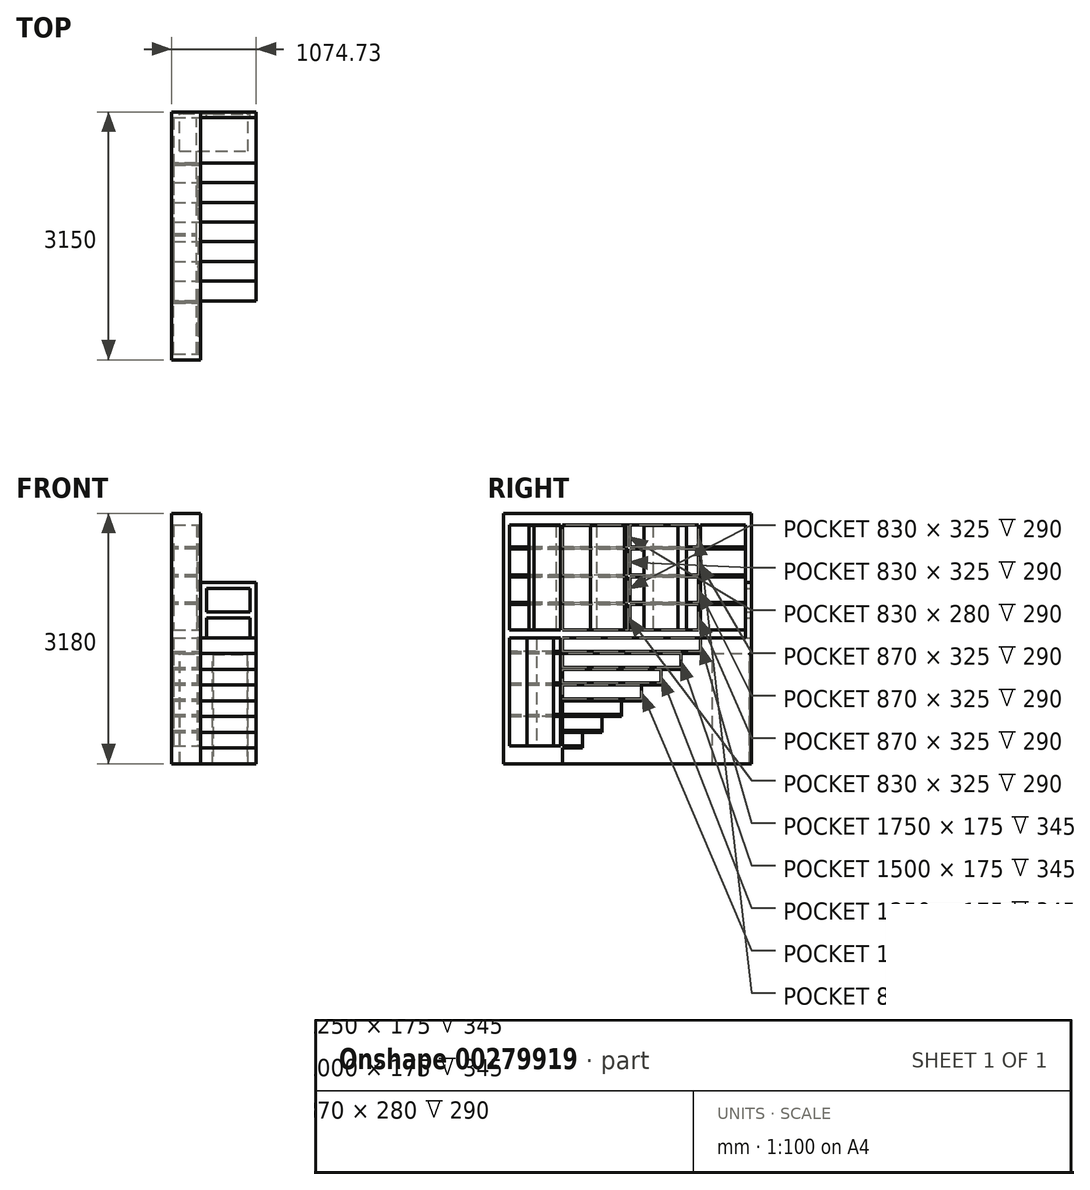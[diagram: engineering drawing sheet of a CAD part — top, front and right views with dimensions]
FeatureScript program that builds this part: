
annotation { "Feature Type Name" : "Feature", "Feature Type Description" : "" }
export const myFeature = defineFeature(function(context is Context, id is Id, definition is map)
    precondition{}
    {
        {
            var Q0;
            Q0=qCreatedBy(makeId("Top.planeOp"),FACE);
            var sketch = newSketch(context, id + "F0", { "sketchPlane" : qUnion([Q0])});
            skLineSegment(sketch, "E0.bottom", {"start": v(0, 0) * mm, "end": v(370, 0) * mm});
            skLineSegment(sketch, "E0.top", {"start": v(0, 3150) * mm, "end": v(370, 3150) * mm});
            skLineSegment(sketch, "E0.left", {"start": v(0, 0) * mm, "end": v(0, 3150) * mm});
            skLineSegment(sketch, "E0.right", {"start": v(370, 0) * mm, "end": v(370, 3150) * mm});
            skLineSegment(sketch, "E1", {"start": v(-177.4, 3270) * mm, "end": v(552.89, 3270) * mm, "construction": true});
            skSolve(sketch);
        }
        {
            var Q0;
            Q0 = qSketchRegion(id + "F0", true);
            extrude(context, id + "F1", {"entities" : qUnion([Q0]), "depth" : 3180 * mm});
        }
        {
            var Q0;
            Q0=makeQuery(id+"F1.opExtrude","SWEPT_FACE",FACE,{"disambiguationData":[OSD([sQuery(id+"F0.wireOp",EDGE,"E0.right")])]});
            var sketch = newSketch(context, id + "F2", { "sketchPlane" : qUnion([Q0])});
            skLineSegment(sketch, "E2.bottom", {"start": v(3150, 0) * mm, "end": v(750, 0) * mm});
            skLineSegment(sketch, "E2.top", {"start": v(2750, 1600) * mm, "end": v(2500, 1600) * mm});
            skLineSegment(sketch, "E2.right", {"start": v(750, 200) * mm, "end": v(750, 0) * mm});
            skLineSegment(sketch, "E3", {"start": v(750, 0) * mm, "end": v(2750, 1600) * mm, "construction": true});
            skLineSegment(sketch, "E4.0.1.0", {"start": v(1000, 200) * mm, "end": v(750, 200) * mm});
            skLineSegment(sketch, "E4.0.2.0", {"start": v(1250, 400) * mm, "end": v(1000, 400) * mm});
            skLineSegment(sketch, "E4.0.3.0", {"start": v(1500, 600) * mm, "end": v(1250, 600) * mm});
            skLineSegment(sketch, "E4.0.4.0", {"start": v(1750, 800) * mm, "end": v(1500, 800) * mm});
            skLineSegment(sketch, "E4.0.5.0", {"start": v(2000, 1000) * mm, "end": v(1750, 1000) * mm});
            skLineSegment(sketch, "E4.0.6.0", {"start": v(2250, 1200) * mm, "end": v(2000, 1200) * mm});
            skLineSegment(sketch, "E4.0.7.0", {"start": v(2500, 1400) * mm, "end": v(2250, 1400) * mm});
            skLineSegment(sketch, "E4.direction1", {"start": v(750, 0) * mm, "end": v(1805.34, 0) * mm, "construction": true});
            skLineSegment(sketch, "E4.direction2", {"start": v(750, 0) * mm, "end": v(750, 200) * mm, "construction": true});
            skLineSegment(sketch, "E5", {"start": v(1000, 200) * mm, "end": v(1000, 400) * mm});
            skLineSegment(sketch, "E6", {"start": v(1250, 400) * mm, "end": v(1250, 600) * mm});
            skLineSegment(sketch, "E7", {"start": v(1500, 600) * mm, "end": v(1500, 800) * mm});
            skLineSegment(sketch, "E8", {"start": v(2000, 1000) * mm, "end": v(2000, 1200) * mm});
            skLineSegment(sketch, "E9", {"start": v(2250, 1200) * mm, "end": v(2250, 1400) * mm});
            skLineSegment(sketch, "E10", {"start": v(2500, 1400) * mm, "end": v(2500, 1600) * mm});
            skLineSegment(sketch, "E11", {"start": v(2750, 1600) * mm, "end": v(3150, 1600) * mm});
            skLineSegment(sketch, "E12", {"start": v(3150, 1600) * mm, "end": v(3150, 0) * mm});
            skLineSegment(sketch, "E13", {"start": v(1750, 800) * mm, "end": v(1750, 1000) * mm});
            skPoint(sketch, "E14.orphan", {"position": v(750, 400) * mm});
            skPoint(sketch, "E15.orphan", {"position": v(750, 600) * mm});
            skPoint(sketch, "E16.orphan", {"position": v(750, 1000) * mm});
            skPoint(sketch, "E17.orphan", {"position": v(750, 1200) * mm});
            skPoint(sketch, "E18.orphan", {"position": v(750, 1400) * mm});
            skPoint(sketch, "E19.orphan", {"position": v(3150, 1400) * mm});
            skPoint(sketch, "E20.orphan", {"position": v(3150, 1200) * mm});
            skPoint(sketch, "E21.orphan", {"position": v(3150, 1000) * mm});
            skPoint(sketch, "E22.orphan", {"position": v(3150, 600) * mm});
            skPoint(sketch, "E23.orphan", {"position": v(3150, 400) * mm});
            skPoint(sketch, "E24.orphan", {"position": v(3150, 200) * mm});
            skPoint(sketch, "E25.orphan", {"position": v(3150, 800) * mm});
            skSolve(sketch);
        }
        {
            var Q0;
            Q0 = qSketchRegion(id + "F2", true);
            extrude(context, id + "F3", {"entities" : qUnion([Q0]), "operationType" : NewBodyOperationType.ADD, "depth" : 700 * mm});
        }
        {
            var Q0;
            Q0=qCreatedBy(makeId("Right.planeOp"),FACE);
            cPlane(context, id + "F4", {"entities" : qUnion([Q0]), "cplaneType" : CPlaneType.OFFSET, "offset" : 25 * mm, "width" : 150 * mm, "height" : 150 * mm});
        }
        {
            var Q0;
            Q0=makeQuery(id+"F1.opExtrude","SWEPT_FACE",FACE,{"disambiguationData":[OSD([sQuery(id+"F0.wireOp",EDGE,"E0.right")])]});
            var sketch = newSketch(context, id + "F5", { "sketchPlane" : qUnion([Q0])});
            skLineSegment(sketch, "E26.bottom", {"start": v(750, 400) * mm, "end": v(1000, 400) * mm});
            skLineSegment(sketch, "E26.top", {"start": v(750, 225) * mm, "end": v(1000, 225) * mm});
            skLineSegment(sketch, "E26.left", {"start": v(750, 400) * mm, "end": v(750, 225) * mm});
            skLineSegment(sketch, "E26.right", {"start": v(1000, 400) * mm, "end": v(1000, 225) * mm});
            skLineSegment(sketch, "E27.0.1.0", {"start": v(1000, 600) * mm, "end": v(1000, 425) * mm});
            skLineSegment(sketch, "E27.0.1.1", {"start": v(750, 600) * mm, "end": v(750, 425) * mm});
            skLineSegment(sketch, "E27.0.1.2", {"start": v(750, 425) * mm, "end": v(1000, 425) * mm});
            skLineSegment(sketch, "E27.0.1.3", {"start": v(750, 600) * mm, "end": v(1000, 600) * mm});
            skLineSegment(sketch, "E27.0.2.0", {"start": v(1000, 800) * mm, "end": v(1000, 625) * mm});
            skLineSegment(sketch, "E27.0.2.1", {"start": v(750, 800) * mm, "end": v(750, 625) * mm});
            skLineSegment(sketch, "E27.0.2.2", {"start": v(750, 625) * mm, "end": v(1000, 625) * mm});
            skLineSegment(sketch, "E27.0.2.3", {"start": v(750, 800) * mm, "end": v(1000, 800) * mm});
            skLineSegment(sketch, "E27.0.3.0", {"start": v(1000, 1000) * mm, "end": v(1000, 825) * mm});
            skLineSegment(sketch, "E27.0.3.1", {"start": v(750, 1000) * mm, "end": v(750, 825) * mm});
            skLineSegment(sketch, "E27.0.3.2", {"start": v(750, 825) * mm, "end": v(1000, 825) * mm});
            skLineSegment(sketch, "E27.0.3.3", {"start": v(750, 1000) * mm, "end": v(1000, 1000) * mm});
            skLineSegment(sketch, "E27.0.4.0", {"start": v(1000, 1200) * mm, "end": v(1000, 1025) * mm});
            skLineSegment(sketch, "E27.0.4.1", {"start": v(750, 1200) * mm, "end": v(750, 1025) * mm});
            skLineSegment(sketch, "E27.0.4.2", {"start": v(750, 1025) * mm, "end": v(1000, 1025) * mm});
            skLineSegment(sketch, "E27.0.4.3", {"start": v(750, 1200) * mm, "end": v(1000, 1200) * mm});
            skLineSegment(sketch, "E27.0.5.0", {"start": v(1000, 1400) * mm, "end": v(1000, 1225) * mm});
            skLineSegment(sketch, "E27.0.5.1", {"start": v(750, 1400) * mm, "end": v(750, 1225) * mm});
            skLineSegment(sketch, "E27.0.5.2", {"start": v(750, 1225) * mm, "end": v(1000, 1225) * mm});
            skLineSegment(sketch, "E27.0.5.3", {"start": v(750, 1400) * mm, "end": v(1000, 1400) * mm});
            skLineSegment(sketch, "E27.0.6.0", {"start": v(1000, 1600) * mm, "end": v(1000, 1425) * mm});
            skLineSegment(sketch, "E27.0.6.1", {"start": v(750, 1600) * mm, "end": v(750, 1425) * mm});
            skLineSegment(sketch, "E27.0.6.2", {"start": v(750, 1425) * mm, "end": v(1000, 1425) * mm});
            skLineSegment(sketch, "E27.0.6.3", {"start": v(750, 1600) * mm, "end": v(1000, 1600) * mm});
            skLineSegment(sketch, "E27.1.1.0", {"start": v(1250, 600) * mm, "end": v(1250, 425) * mm});
            skLineSegment(sketch, "E27.1.1.1", {"start": v(1000, 600) * mm, "end": v(1000, 425) * mm});
            skLineSegment(sketch, "E27.1.1.2", {"start": v(1000, 425) * mm, "end": v(1250, 425) * mm});
            skLineSegment(sketch, "E27.1.1.3", {"start": v(1000, 600) * mm, "end": v(1250, 600) * mm});
            skLineSegment(sketch, "E27.1.2.0", {"start": v(1250, 800) * mm, "end": v(1250, 625) * mm});
            skLineSegment(sketch, "E27.1.2.1", {"start": v(1000, 800) * mm, "end": v(1000, 625) * mm});
            skLineSegment(sketch, "E27.1.2.2", {"start": v(1000, 625) * mm, "end": v(1250, 625) * mm});
            skLineSegment(sketch, "E27.1.2.3", {"start": v(1000, 800) * mm, "end": v(1250, 800) * mm});
            skLineSegment(sketch, "E27.1.3.0", {"start": v(1250, 1000) * mm, "end": v(1250, 825) * mm});
            skLineSegment(sketch, "E27.1.3.1", {"start": v(1000, 1000) * mm, "end": v(1000, 825) * mm});
            skLineSegment(sketch, "E27.1.3.2", {"start": v(1000, 825) * mm, "end": v(1250, 825) * mm});
            skLineSegment(sketch, "E27.1.3.3", {"start": v(1000, 1000) * mm, "end": v(1250, 1000) * mm});
            skLineSegment(sketch, "E27.1.4.0", {"start": v(1250, 1200) * mm, "end": v(1250, 1025) * mm});
            skLineSegment(sketch, "E27.1.4.1", {"start": v(1000, 1200) * mm, "end": v(1000, 1025) * mm});
            skLineSegment(sketch, "E27.1.4.2", {"start": v(1000, 1025) * mm, "end": v(1250, 1025) * mm});
            skLineSegment(sketch, "E27.1.4.3", {"start": v(1000, 1200) * mm, "end": v(1250, 1200) * mm});
            skLineSegment(sketch, "E27.1.5.0", {"start": v(1250, 1400) * mm, "end": v(1250, 1225) * mm});
            skLineSegment(sketch, "E27.1.5.1", {"start": v(1000, 1400) * mm, "end": v(1000, 1225) * mm});
            skLineSegment(sketch, "E27.1.5.2", {"start": v(1000, 1225) * mm, "end": v(1250, 1225) * mm});
            skLineSegment(sketch, "E27.1.5.3", {"start": v(1000, 1400) * mm, "end": v(1250, 1400) * mm});
            skLineSegment(sketch, "E27.1.6.0", {"start": v(1250, 1600) * mm, "end": v(1250, 1425) * mm});
            skLineSegment(sketch, "E27.1.6.1", {"start": v(1000, 1600) * mm, "end": v(1000, 1425) * mm});
            skLineSegment(sketch, "E27.1.6.2", {"start": v(1000, 1425) * mm, "end": v(1250, 1425) * mm});
            skLineSegment(sketch, "E27.1.6.3", {"start": v(1000, 1600) * mm, "end": v(1250, 1600) * mm});
            skLineSegment(sketch, "E27.2.1.1", {"start": v(1250, 600) * mm, "end": v(1250, 425) * mm});
            skLineSegment(sketch, "E27.2.1.3", {"start": v(1250, 600) * mm, "end": v(1500, 600) * mm});
            skLineSegment(sketch, "E27.2.2.0", {"start": v(1500, 800) * mm, "end": v(1500, 625) * mm});
            skLineSegment(sketch, "E27.2.2.1", {"start": v(1250, 800) * mm, "end": v(1250, 625) * mm});
            skLineSegment(sketch, "E27.2.2.2", {"start": v(1250, 625) * mm, "end": v(1500, 625) * mm});
            skLineSegment(sketch, "E27.2.2.3", {"start": v(1250, 800) * mm, "end": v(1500, 800) * mm});
            skLineSegment(sketch, "E27.2.3.0", {"start": v(1500, 1000) * mm, "end": v(1500, 825) * mm});
            skLineSegment(sketch, "E27.2.3.1", {"start": v(1250, 1000) * mm, "end": v(1250, 825) * mm});
            skLineSegment(sketch, "E27.2.3.2", {"start": v(1250, 825) * mm, "end": v(1500, 825) * mm});
            skLineSegment(sketch, "E27.2.3.3", {"start": v(1250, 1000) * mm, "end": v(1500, 1000) * mm});
            skLineSegment(sketch, "E27.2.4.0", {"start": v(1500, 1200) * mm, "end": v(1500, 1025) * mm});
            skLineSegment(sketch, "E27.2.4.1", {"start": v(1250, 1200) * mm, "end": v(1250, 1025) * mm});
            skLineSegment(sketch, "E27.2.4.2", {"start": v(1250, 1025) * mm, "end": v(1500, 1025) * mm});
            skLineSegment(sketch, "E27.2.4.3", {"start": v(1250, 1200) * mm, "end": v(1500, 1200) * mm});
            skLineSegment(sketch, "E27.2.5.0", {"start": v(1500, 1400) * mm, "end": v(1500, 1225) * mm});
            skLineSegment(sketch, "E27.2.5.1", {"start": v(1250, 1400) * mm, "end": v(1250, 1225) * mm});
            skLineSegment(sketch, "E27.2.5.2", {"start": v(1250, 1225) * mm, "end": v(1500, 1225) * mm});
            skLineSegment(sketch, "E27.2.5.3", {"start": v(1250, 1400) * mm, "end": v(1500, 1400) * mm});
            skLineSegment(sketch, "E27.2.6.0", {"start": v(1500, 1600) * mm, "end": v(1500, 1425) * mm});
            skLineSegment(sketch, "E27.2.6.1", {"start": v(1250, 1600) * mm, "end": v(1250, 1425) * mm});
            skLineSegment(sketch, "E27.2.6.2", {"start": v(1250, 1425) * mm, "end": v(1500, 1425) * mm});
            skLineSegment(sketch, "E27.2.6.3", {"start": v(1250, 1600) * mm, "end": v(1500, 1600) * mm});
            skLineSegment(sketch, "E27.3.2.1", {"start": v(1500, 800) * mm, "end": v(1500, 625) * mm});
            skLineSegment(sketch, "E27.3.2.3", {"start": v(1500, 800) * mm, "end": v(1750, 800) * mm});
            skLineSegment(sketch, "E27.3.3.0", {"start": v(1750, 1000) * mm, "end": v(1750, 825) * mm});
            skLineSegment(sketch, "E27.3.3.1", {"start": v(1500, 1000) * mm, "end": v(1500, 825) * mm});
            skLineSegment(sketch, "E27.3.3.2", {"start": v(1500, 825) * mm, "end": v(1750, 825) * mm});
            skLineSegment(sketch, "E27.3.3.3", {"start": v(1500, 1000) * mm, "end": v(1750, 1000) * mm});
            skLineSegment(sketch, "E27.3.4.0", {"start": v(1750, 1200) * mm, "end": v(1750, 1025) * mm});
            skLineSegment(sketch, "E27.3.4.1", {"start": v(1500, 1200) * mm, "end": v(1500, 1025) * mm});
            skLineSegment(sketch, "E27.3.4.2", {"start": v(1500, 1025) * mm, "end": v(1750, 1025) * mm});
            skLineSegment(sketch, "E27.3.4.3", {"start": v(1500, 1200) * mm, "end": v(1750, 1200) * mm});
            skLineSegment(sketch, "E27.3.5.0", {"start": v(1750, 1400) * mm, "end": v(1750, 1225) * mm});
            skLineSegment(sketch, "E27.3.5.1", {"start": v(1500, 1400) * mm, "end": v(1500, 1225) * mm});
            skLineSegment(sketch, "E27.3.5.2", {"start": v(1500, 1225) * mm, "end": v(1750, 1225) * mm});
            skLineSegment(sketch, "E27.3.5.3", {"start": v(1500, 1400) * mm, "end": v(1750, 1400) * mm});
            skLineSegment(sketch, "E27.3.6.0", {"start": v(1750, 1600) * mm, "end": v(1750, 1425) * mm});
            skLineSegment(sketch, "E27.3.6.1", {"start": v(1500, 1600) * mm, "end": v(1500, 1425) * mm});
            skLineSegment(sketch, "E27.3.6.2", {"start": v(1500, 1425) * mm, "end": v(1750, 1425) * mm});
            skLineSegment(sketch, "E27.3.6.3", {"start": v(1500, 1600) * mm, "end": v(1750, 1600) * mm});
            skLineSegment(sketch, "E27.4.3.1", {"start": v(1750, 1000) * mm, "end": v(1750, 825) * mm});
            skLineSegment(sketch, "E27.4.3.3", {"start": v(1750, 1000) * mm, "end": v(2000, 1000) * mm});
            skLineSegment(sketch, "E27.4.4.0", {"start": v(2000, 1200) * mm, "end": v(2000, 1025) * mm});
            skLineSegment(sketch, "E27.4.4.1", {"start": v(1750, 1200) * mm, "end": v(1750, 1025) * mm});
            skLineSegment(sketch, "E27.4.4.2", {"start": v(1750, 1025) * mm, "end": v(2000, 1025) * mm});
            skLineSegment(sketch, "E27.4.4.3", {"start": v(1750, 1200) * mm, "end": v(2000, 1200) * mm});
            skLineSegment(sketch, "E27.4.5.0", {"start": v(2000, 1400) * mm, "end": v(2000, 1225) * mm});
            skLineSegment(sketch, "E27.4.5.1", {"start": v(1750, 1400) * mm, "end": v(1750, 1225) * mm});
            skLineSegment(sketch, "E27.4.5.2", {"start": v(1750, 1225) * mm, "end": v(2000, 1225) * mm});
            skLineSegment(sketch, "E27.4.5.3", {"start": v(1750, 1400) * mm, "end": v(2000, 1400) * mm});
            skLineSegment(sketch, "E27.4.6.0", {"start": v(2000, 1600) * mm, "end": v(2000, 1425) * mm});
            skLineSegment(sketch, "E27.4.6.1", {"start": v(1750, 1600) * mm, "end": v(1750, 1425) * mm});
            skLineSegment(sketch, "E27.4.6.2", {"start": v(1750, 1425) * mm, "end": v(2000, 1425) * mm});
            skLineSegment(sketch, "E27.4.6.3", {"start": v(1750, 1600) * mm, "end": v(2000, 1600) * mm});
            skLineSegment(sketch, "E27.5.4.1", {"start": v(2000, 1200) * mm, "end": v(2000, 1025) * mm});
            skLineSegment(sketch, "E27.5.4.3", {"start": v(2000, 1200) * mm, "end": v(2250, 1200) * mm});
            skLineSegment(sketch, "E27.5.5.0", {"start": v(2250, 1400) * mm, "end": v(2250, 1225) * mm});
            skLineSegment(sketch, "E27.5.5.1", {"start": v(2000, 1400) * mm, "end": v(2000, 1225) * mm});
            skLineSegment(sketch, "E27.5.5.2", {"start": v(2000, 1225) * mm, "end": v(2250, 1225) * mm});
            skLineSegment(sketch, "E27.5.5.3", {"start": v(2000, 1400) * mm, "end": v(2250, 1400) * mm});
            skLineSegment(sketch, "E27.5.6.0", {"start": v(2250, 1600) * mm, "end": v(2250, 1425) * mm});
            skLineSegment(sketch, "E27.5.6.1", {"start": v(2000, 1600) * mm, "end": v(2000, 1425) * mm});
            skLineSegment(sketch, "E27.5.6.2", {"start": v(2000, 1425) * mm, "end": v(2250, 1425) * mm});
            skLineSegment(sketch, "E27.5.6.3", {"start": v(2000, 1600) * mm, "end": v(2250, 1600) * mm});
            skLineSegment(sketch, "E27.6.5.1", {"start": v(2250, 1400) * mm, "end": v(2250, 1225) * mm});
            skLineSegment(sketch, "E27.6.5.3", {"start": v(2250, 1400) * mm, "end": v(2500, 1400) * mm});
            skLineSegment(sketch, "E27.6.6.0", {"start": v(2500, 1600) * mm, "end": v(2500, 1425) * mm});
            skLineSegment(sketch, "E27.6.6.1", {"start": v(2250, 1600) * mm, "end": v(2250, 1425) * mm});
            skLineSegment(sketch, "E27.6.6.2", {"start": v(2250, 1425) * mm, "end": v(2500, 1425) * mm});
            skLineSegment(sketch, "E27.6.6.3", {"start": v(2250, 1600) * mm, "end": v(2500, 1600) * mm});
            skLineSegment(sketch, "E27.direction1", {"start": v(750, 225) * mm, "end": v(1000, 225) * mm, "construction": true});
            skLineSegment(sketch, "E27.direction2", {"start": v(750, 225) * mm, "end": v(750, 425) * mm, "construction": true});
            skSolve(sketch);
        }
        {
            var Q0;
            Q0 = qSketchRegion(id + "F5", true);
            var Q1;
            Q1=qCreatedBy(id+"F4.planeOp",FACE);
            extrude(context, id + "F6", {"entities" : qUnion([Q0]), "operationType" : NewBodyOperationType.REMOVE, "endBound" : BoundingType.UP_TO_SURFACE, "oppositeDirection" : true, "endBoundEntityFace" : qUnion([Q1]), "depth" : 25 * mm});
        }
        {
            var Q0;
            Q0=makeQuery(id+"F1.opExtrude","SWEPT_FACE",FACE,{"disambiguationData":[OSD([sQuery(id+"F0.wireOp",EDGE,"E0.right")])]});
            var sketch = newSketch(context, id + "F7", { "sketchPlane" : qUnion([Q0])});
            skLineSegment(sketch, "E28.bottom", {"start": v(725, 225) * mm, "end": v(75, 225) * mm});
            skLineSegment(sketch, "E28.top", {"start": v(725, 600) * mm, "end": v(75, 600) * mm});
            skLineSegment(sketch, "E28.left", {"start": v(725, 225) * mm, "end": v(725, 600) * mm});
            skLineSegment(sketch, "E28.right", {"start": v(75, 225) * mm, "end": v(75, 600) * mm});
            skLineSegment(sketch, "E29.0.1.0", {"start": v(725, 625) * mm, "end": v(75, 625) * mm});
            skLineSegment(sketch, "E29.0.1.1", {"start": v(725, 1000) * mm, "end": v(75, 1000) * mm});
            skLineSegment(sketch, "E29.0.1.2", {"start": v(725, 625) * mm, "end": v(725, 1000) * mm});
            skLineSegment(sketch, "E29.0.1.3", {"start": v(75, 625) * mm, "end": v(75, 1000) * mm});
            skLineSegment(sketch, "E29.0.2.0", {"start": v(725, 1025) * mm, "end": v(75, 1025) * mm});
            skLineSegment(sketch, "E29.0.2.1", {"start": v(725, 1400) * mm, "end": v(75, 1400) * mm});
            skLineSegment(sketch, "E29.0.2.2", {"start": v(725, 1025) * mm, "end": v(725, 1400) * mm});
            skLineSegment(sketch, "E29.0.2.3", {"start": v(75, 1025) * mm, "end": v(75, 1400) * mm});
            skLineSegment(sketch, "E29.direction1", {"start": v(50, 225) * mm, "end": v(75, 225) * mm, "construction": true});
            skLineSegment(sketch, "E29.direction2", {"start": v(75, 225) * mm, "end": v(75, 625) * mm, "construction": true});
            skLineSegment(sketch, "E30.bottom", {"start": v(725, 1425) * mm, "end": v(75, 1425) * mm});
            skLineSegment(sketch, "E30.top", {"start": v(725, 1600) * mm, "end": v(75, 1600) * mm});
            skLineSegment(sketch, "E30.left", {"start": v(725, 1425) * mm, "end": v(725, 1600) * mm});
            skLineSegment(sketch, "E30.right", {"start": v(75, 1425) * mm, "end": v(75, 1600) * mm});
            skSolve(sketch);
        }
        {
            var Q0;
            Q0 = qSketchRegion(id + "F7", true);
            var Q1;
            Q1=qCreatedBy(id+"F4.planeOp",FACE);
            extrude(context, id + "F8", {"entities" : qUnion([Q0]), "operationType" : NewBodyOperationType.REMOVE, "endBound" : BoundingType.UP_TO_SURFACE, "oppositeDirection" : true, "endBoundEntityFace" : qUnion([Q1]), "depth" : 25 * mm});
        }
        {
            var Q0;
            Q0=makeQuery(id+"F1.opExtrude","SWEPT_FACE",FACE,{"disambiguationData":[OSD([sQuery(id+"F0.wireOp",EDGE,"E0.right")])]});
            var sketch = newSketch(context, id + "F9", { "sketchPlane" : qUnion([Q0])});
            skLineSegment(sketch, "E31.bottom", {"start": v(2500, 1700) * mm, "end": v(3075, 1700) * mm});
            skLineSegment(sketch, "E31.top", {"start": v(2500, 3030) * mm, "end": v(3075, 3030) * mm});
            skLineSegment(sketch, "E31.left", {"start": v(2500, 1700) * mm, "end": v(2500, 3030) * mm});
            skLineSegment(sketch, "E31.right", {"start": v(3075, 1700) * mm, "end": v(3075, 3030) * mm});
            skLineSegment(sketch, "E32.bottom", {"start": v(725, 1700) * mm, "end": v(75, 1700) * mm});
            skLineSegment(sketch, "E32.top", {"start": v(725, 3030) * mm, "end": v(75, 3030) * mm});
            skLineSegment(sketch, "E32.left", {"start": v(725, 1700) * mm, "end": v(725, 3030) * mm});
            skLineSegment(sketch, "E32.right", {"start": v(75, 1700) * mm, "end": v(75, 3030) * mm});
            skLineSegment(sketch, "E33.bottom", {"start": v(750, 1700) * mm, "end": v(2475, 1700) * mm});
            skLineSegment(sketch, "E33.top", {"start": v(750, 3030) * mm, "end": v(2475, 3030) * mm});
            skLineSegment(sketch, "E33.left", {"start": v(750, 1700) * mm, "end": v(750, 3030) * mm});
            skLineSegment(sketch, "E33.right", {"start": v(2475, 1700) * mm, "end": v(2475, 3030) * mm});
            skSolve(sketch);
        }
        {
            var Q0;
            Q0=makeQuery(id+"F9.imprint","IMPRINT",FACE,{"disambiguationData":[TD([[makeQuery(id+"F9.imprint","IMPRINT",EDGE,{"derivedFrom":sQuery(id+"F9.wireOp",EDGE,"E31.bottom")}),-1.0]])]});
            var sketch = newSketch(context, id + "F10", { "sketchPlane" : qUnion([Q0])});
            skLineSegment(sketch, "E34.bottom", {"start": v(75, 1425) * mm, "end": v(725, 1425) * mm});
            skLineSegment(sketch, "E34.top", {"start": v(75, 600) * mm, "end": v(725, 600) * mm});
            skLineSegment(sketch, "E34.left", {"start": v(75, 1425) * mm, "end": v(75, 600) * mm});
            skLineSegment(sketch, "E34.right", {"start": v(725, 1425) * mm, "end": v(725, 600) * mm});
            skSolve(sketch);
        }
        {
            var Q0;
            Q0 = qSketchRegion(id + "F10", true);
            extrude(context, id + "F11", {"entities" : qUnion([Q0]), "operationType" : NewBodyOperationType.REMOVE, "oppositeDirection" : true, "depth" : 55 * mm});
        }
        {
            var Q0;
            Q0 = qSketchRegion(id + "F9", true);
            var Q1;
            Q1=qCreatedBy(id+"F4.planeOp",FACE);
            extrude(context, id + "F12", {"entities" : qUnion([Q0]), "operationType" : NewBodyOperationType.REMOVE, "endBound" : BoundingType.UP_TO_SURFACE, "oppositeDirection" : true, "endBoundEntityFace" : qUnion([Q1]), "depth" : 25 * mm});
        }
        {
            var Q0;
            {var subQ0=sQuery(id+"F10.wireOp",EDGE,"E34.left");var subQ1=sQuery(id+"F10.wireOp",EDGE,"E34.right");Q0=makeQuery(id+"F11.boolean.opBoolean","COPY",FACE,{"disambiguationData":[TD([makeQuery(id+"F8.boolean.opBoolean","COPY",FACE,{"derivedFrom":makeQuery(id+"F8.opExtrude","SWEPT_FACE",FACE,{"disambiguationData":[OSD([sQuery(id+"F7.wireOp",EDGE,"E29.0.2.1")])]})})])],"derivedFrom":makeQuery(id+"F11.opExtrude","CAP_FACE",FACE,{"disambiguationData":[OSD([sQuery(id+"F10.wireOp",EDGE,"E34.bottom"),sQuery(id+"F10.wireOp",EDGE,"E34.top"),subQ0,subQ1])],"isStart":false})});}
            var sketch = newSketch(context, id + "F13", { "sketchPlane" : qUnion([Q0])});
            skLineSegment(sketch, "E35.bottom", {"start": v(75, 2025) * mm, "end": v(1580, 2025) * mm});
            skLineSegment(sketch, "E35.top", {"start": v(75, 2050) * mm, "end": v(1580, 2050) * mm});
            skLineSegment(sketch, "E35.left", {"start": v(75, 2025) * mm, "end": v(75, 2050) * mm});
            skLineSegment(sketch, "E35.right", {"start": v(3075, 2025) * mm, "end": v(3075, 2050) * mm});
            skLineSegment(sketch, "E36.0.1.0", {"start": v(75, 2400) * mm, "end": v(1580, 2400) * mm});
            skLineSegment(sketch, "E36.0.1.1", {"start": v(75, 2375) * mm, "end": v(1580, 2375) * mm});
            skLineSegment(sketch, "E36.0.1.2", {"start": v(3075, 2375) * mm, "end": v(3075, 2400) * mm});
            skLineSegment(sketch, "E36.0.1.3", {"start": v(75, 2375) * mm, "end": v(75, 2400) * mm});
            skLineSegment(sketch, "E36.0.2.0", {"start": v(75, 2750) * mm, "end": v(1580, 2750) * mm});
            skLineSegment(sketch, "E36.0.2.1", {"start": v(75, 2725) * mm, "end": v(1580, 2725) * mm});
            skLineSegment(sketch, "E36.0.2.2", {"start": v(3075, 2725) * mm, "end": v(3075, 2750) * mm});
            skLineSegment(sketch, "E36.0.2.3", {"start": v(75, 2725) * mm, "end": v(75, 2750) * mm});
            skLineSegment(sketch, "E36.direction1", {"start": v(75, 2020) * mm, "end": v(100, 2020) * mm, "construction": true});
            skLineSegment(sketch, "E36.direction2", {"start": v(75, 2020) * mm, "end": v(75, 2370) * mm, "construction": true});
            skLineSegment(sketch, "E37.bottom", {"start": v(1580, 3030) * mm, "end": v(1605, 3030) * mm});
            skLineSegment(sketch, "E37.top", {"start": v(1580, 1700) * mm, "end": v(1605, 1700) * mm});
            skLineSegment(sketch, "E37.left", {"start": v(1580, 3030) * mm, "end": v(1580, 1700) * mm});
            skLineSegment(sketch, "E37.right", {"start": v(1605, 3030) * mm, "end": v(1605, 1700) * mm});
            skLineSegment(sketch, "E38.trimOffspring", {"start": v(1605, 2050) * mm, "end": v(3075, 2050) * mm});
            skLineSegment(sketch, "E39.trimOffspring", {"start": v(1605, 2025) * mm, "end": v(3075, 2025) * mm});
            skLineSegment(sketch, "E40.trimOffspring", {"start": v(1605, 2400) * mm, "end": v(3075, 2400) * mm});
            skLineSegment(sketch, "E41.trimOffspring", {"start": v(1605, 2375) * mm, "end": v(3075, 2375) * mm});
            skLineSegment(sketch, "E42.trimOffspring", {"start": v(1605, 2750) * mm, "end": v(3075, 2750) * mm});
            skLineSegment(sketch, "E43.trimOffspring", {"start": v(1605, 2725) * mm, "end": v(3075, 2725) * mm});
            skSolve(sketch);
        }
        {
            var Q0;
            Q0 = qSketchRegion(id + "F13", true);
            var Q1;
            Q1=qCreatedBy(id+"F4.planeOp",FACE);
            extrude(context, id + "F14", {"entities" : qUnion([Q0]), "operationType" : NewBodyOperationType.ADD, "endBound" : BoundingType.UP_TO_SURFACE, "oppositeDirection" : true, "endBoundEntityFace" : qUnion([Q1]), "depth" : 25 * mm});
        }
        {
            var Q0;
            Q0=makeQuery(id+"F1.opExtrude","SWEPT_FACE",FACE,{"disambiguationData":[OSD([sQuery(id+"F0.wireOp",EDGE,"E0.right")])]});
            cPlane(context, id + "F15", {"entities" : qUnion([Q0]), "cplaneType" : CPlaneType.OFFSET, "offset" : 25 * mm, "oppositeDirection" : true, "width" : 150 * mm, "height" : 150 * mm});
        }
        {
            var Q0;
            Q0=qCreatedBy(id+"F15.planeOp",FACE);
            cPlane(context, id + "F16", {"entities" : qUnion([Q0]), "cplaneType" : CPlaneType.OFFSET, "offset" : 25 * mm, "oppositeDirection" : true, "width" : 150 * mm, "height" : 150 * mm});
        }
        {
            var Q0;
            Q0=qCreatedBy(id+"F16.planeOp",FACE);
            var sketch = newSketch(context, id + "F17", { "sketchPlane" : qUnion([Q0])});
            skLineSegment(sketch, "E44.bottom", {"start": v(75, 1595) * mm, "end": v(415, 1595) * mm});
            skLineSegment(sketch, "E44.top", {"start": v(75, 225) * mm, "end": v(415, 225) * mm});
            skLineSegment(sketch, "E44.left", {"start": v(75, 1595) * mm, "end": v(75, 225) * mm});
            skLineSegment(sketch, "E44.right", {"start": v(415, 1595) * mm, "end": v(415, 225) * mm});
            skLineSegment(sketch, "E45.bottom", {"start": v(325, 3025) * mm, "end": v(665, 3025) * mm});
            skLineSegment(sketch, "E45.top", {"start": v(325, 1700) * mm, "end": v(665, 1700) * mm});
            skLineSegment(sketch, "E45.left", {"start": v(325, 3025) * mm, "end": v(325, 1700) * mm});
            skLineSegment(sketch, "E45.right", {"start": v(665, 3025) * mm, "end": v(665, 1700) * mm});
            skLineSegment(sketch, "E46.bottom", {"start": v(750, 3025) * mm, "end": v(1180, 3025) * mm});
            skLineSegment(sketch, "E46.top", {"start": v(750, 1700) * mm, "end": v(1180, 1700) * mm});
            skLineSegment(sketch, "E46.left", {"start": v(750, 3025) * mm, "end": v(750, 1700) * mm});
            skLineSegment(sketch, "E46.right", {"start": v(1180, 3025) * mm, "end": v(1180, 1700) * mm});
            skLineSegment(sketch, "E47.bottom", {"start": v(2325, 3025) * mm, "end": v(1895, 3025) * mm});
            skLineSegment(sketch, "E47.top", {"start": v(2325, 1700) * mm, "end": v(1895, 1700) * mm});
            skLineSegment(sketch, "E47.left", {"start": v(2325, 3025) * mm, "end": v(2325, 1700) * mm});
            skLineSegment(sketch, "E47.right", {"start": v(1895, 3025) * mm, "end": v(1895, 1700) * mm});
            skSolve(sketch);
        }
        {
            var Q0;
            Q0 = qSketchRegion(id + "F17", true);
            extrude(context, id + "F18", {"entities" : qUnion([Q0]), "operationType" : NewBodyOperationType.ADD, "depth" : 20 * mm});
        }
        {
            var Q0;
            Q0=qCreatedBy(id+"F15.planeOp",FACE);
            var sketch = newSketch(context, id + "F19", { "sketchPlane" : qUnion([Q0])});
            skLineSegment(sketch, "E48.bottom", {"start": v(295, 1595) * mm, "end": v(635, 1595) * mm});
            skLineSegment(sketch, "E48.top", {"start": v(295, 225) * mm, "end": v(635, 225) * mm});
            skLineSegment(sketch, "E48.left", {"start": v(295, 1595) * mm, "end": v(295, 225) * mm});
            skLineSegment(sketch, "E48.right", {"start": v(635, 1595) * mm, "end": v(635, 225) * mm});
            skLineSegment(sketch, "E49.bottom", {"start": v(385, 3025) * mm, "end": v(725, 3025) * mm});
            skLineSegment(sketch, "E49.top", {"start": v(385, 1700) * mm, "end": v(725, 1700) * mm});
            skLineSegment(sketch, "E49.left", {"start": v(385, 3025) * mm, "end": v(385, 1700) * mm});
            skLineSegment(sketch, "E49.right", {"start": v(725, 3025) * mm, "end": v(725, 1700) * mm});
            skLineSegment(sketch, "E50.bottom", {"start": v(1105, 3025) * mm, "end": v(1535, 3025) * mm});
            skLineSegment(sketch, "E50.top", {"start": v(1105, 1700) * mm, "end": v(1535, 1700) * mm});
            skLineSegment(sketch, "E50.left", {"start": v(1105, 3025) * mm, "end": v(1105, 1700) * mm});
            skLineSegment(sketch, "E50.right", {"start": v(1535, 3025) * mm, "end": v(1535, 1700) * mm});
            skLineSegment(sketch, "E51.bottom", {"start": v(1785, 3025) * mm, "end": v(2215, 3025) * mm});
            skLineSegment(sketch, "E51.top", {"start": v(1785, 1700) * mm, "end": v(2215, 1700) * mm});
            skLineSegment(sketch, "E51.left", {"start": v(1785, 3025) * mm, "end": v(1785, 1700) * mm});
            skLineSegment(sketch, "E51.right", {"start": v(2215, 3025) * mm, "end": v(2215, 1700) * mm});
            skSolve(sketch);
        }
        {
            var Q0;
            Q0 = qSketchRegion(id + "F19", true);
            extrude(context, id + "F20", {"entities" : qUnion([Q0]), "operationType" : NewBodyOperationType.ADD, "depth" : 20 * mm});
        }
        {
            var Q0;
            Q0=makeQuery(id+"F3.boolean.opBoolean","MERGE",FACE,{"derivedFrom":[makeQuery(id+"F1.opExtrude","SWEPT_FACE",FACE,{"disambiguationData":[OSD([sQuery(id+"F0.wireOp",EDGE,"E0.top")])]}),makeQuery(id+"F3.opExtrude","SWEPT_FACE",FACE,{"disambiguationData":[OSD([sQuery(id+"F2.wireOp",EDGE,"E12")])]})]});
            var sketch = newSketch(context, id + "F21", { "sketchPlane" : qUnion([Q0])});
            skLineSegment(sketch, "E52.bottom", {"start": v(-1070, 1600) * mm, "end": v(-995, 1600) * mm});
            skLineSegment(sketch, "E52.top", {"start": v(-1070, 2300) * mm, "end": v(-370, 2300) * mm});
            skLineSegment(sketch, "E52.left", {"start": v(-1070, 1600) * mm, "end": v(-1070, 2300) * mm});
            skLineSegment(sketch, "E52.right", {"start": v(-370, 1600) * mm, "end": v(-370, 2300) * mm});
            skLineSegment(sketch, "E53.top", {"start": v(-995, 2225) * mm, "end": v(-445, 2225) * mm});
            skLineSegment(sketch, "E53.left", {"start": v(-995, 1600) * mm, "end": v(-995, 1850) * mm});
            skLineSegment(sketch, "E53.right", {"start": v(-445, 1600) * mm, "end": v(-445, 1850) * mm});
            skLineSegment(sketch, "E54.bottom", {"start": v(-995, 1925) * mm, "end": v(-445, 1925) * mm});
            skLineSegment(sketch, "E54.top", {"start": v(-995, 1850) * mm, "end": v(-445, 1850) * mm});
            skLineSegment(sketch, "E55.trimOffspring", {"start": v(-995, 1925) * mm, "end": v(-995, 2225) * mm});
            skLineSegment(sketch, "E56.trimOffspring", {"start": v(-445, 1925) * mm, "end": v(-445, 2225) * mm});
            skLineSegment(sketch, "E57.trimOffspring", {"start": v(-445, 1600) * mm, "end": v(-370, 1600) * mm});
            skSolve(sketch);
        }
        {
            var Q0;
            Q0 = qSketchRegion(id + "F21", true);
            var Q1;
            Q1=makeQuery(id+"F12.boolean.opBoolean","COPY",FACE,{"derivedFrom":makeQuery(id+"F12.opExtrude","SWEPT_FACE",FACE,{"disambiguationData":[OSD([sQuery(id+"F9.wireOp",EDGE,"E31.right")])]})});
            extrude(context, id + "F22", {"entities" : qUnion([Q0]), "operationType" : NewBodyOperationType.ADD, "endBound" : BoundingType.UP_TO_SURFACE, "oppositeDirection" : true, "endBoundEntityFace" : qUnion([Q1]), "depth" : 25 * mm});
        }
        {
            var Q0;
            Q0=makeQuery(id+"F22.boolean.opBoolean","MERGE",FACE,{"derivedFrom":[makeQuery(id+"F3.boolean.opBoolean","MERGE",FACE,{"derivedFrom":[makeQuery(id+"F1.opExtrude","SWEPT_FACE",FACE,{"disambiguationData":[OSD([sQuery(id+"F0.wireOp",EDGE,"E0.top")])]}),makeQuery(id+"F3.opExtrude","SWEPT_FACE",FACE,{"disambiguationData":[OSD([sQuery(id+"F2.wireOp",EDGE,"E12")])]})]}),makeQuery(id+"F22.opExtrude","CAP_FACE",FACE,{"disambiguationData":[OSD([sQuery(id+"F21.wireOp",EDGE,"E52.bottom"),sQuery(id+"F21.wireOp",EDGE,"E52.top"),sQuery(id+"F21.wireOp",EDGE,"E52.left"),sQuery(id+"F21.wireOp",EDGE,"E52.right"),sQuery(id+"F21.wireOp",EDGE,"E53.top"),sQuery(id+"F21.wireOp",EDGE,"E53.left"),sQuery(id+"F21.wireOp",EDGE,"E53.right"),sQuery(id+"F21.wireOp",EDGE,"E54.bottom"),sQuery(id+"F21.wireOp",EDGE,"E54.top"),sQuery(id+"F21.wireOp",EDGE,"E55.trimOffspring"),sQuery(id+"F21.wireOp",EDGE,"E56.trimOffspring"),sQuery(id+"F21.wireOp",EDGE,"E57.trimOffspring")])],"isStart":true})]});
            var sketch = newSketch(context, id + "F23", { "sketchPlane" : qUnion([Q0])});
            skLineSegment(sketch, "E58.bottom", {"start": v(-970, 0) * mm, "end": v(-100, 0) * mm});
            skLineSegment(sketch, "E58.top", {"start": v(-970, 1400) * mm, "end": v(-100, 1400) * mm});
            skLineSegment(sketch, "E58.left", {"start": v(-970, 0) * mm, "end": v(-970, 1400) * mm});
            skLineSegment(sketch, "E58.right", {"start": v(-100, 0) * mm, "end": v(-100, 1400) * mm});
            skSolve(sketch);
        }
        {
            var Q0;
            Q0 = qSketchRegion(id + "F23", true);
            extrude(context, id + "F24", {"entities" : qUnion([Q0]), "operationType" : NewBodyOperationType.REMOVE, "oppositeDirection" : true, "depth" : 500 * mm});
        }
        {
            var Q0;
            Q0=makeQuery(id+"F22.boolean.opBoolean","MERGE",FACE,{"derivedFrom":[makeQuery(id+"F3.boolean.opBoolean","MERGE",FACE,{"derivedFrom":[makeQuery(id+"F1.opExtrude","SWEPT_FACE",FACE,{"disambiguationData":[OSD([sQuery(id+"F0.wireOp",EDGE,"E0.top")])]}),makeQuery(id+"F3.opExtrude","SWEPT_FACE",FACE,{"disambiguationData":[OSD([sQuery(id+"F2.wireOp",EDGE,"E12")])]})]}),makeQuery(id+"F22.opExtrude","CAP_FACE",FACE,{"disambiguationData":[OSD([sQuery(id+"F21.wireOp",EDGE,"E52.bottom"),sQuery(id+"F21.wireOp",EDGE,"E52.top"),sQuery(id+"F21.wireOp",EDGE,"E52.left"),sQuery(id+"F21.wireOp",EDGE,"E52.right"),sQuery(id+"F21.wireOp",EDGE,"E53.top"),sQuery(id+"F21.wireOp",EDGE,"E53.left"),sQuery(id+"F21.wireOp",EDGE,"E53.right"),sQuery(id+"F21.wireOp",EDGE,"E54.bottom"),sQuery(id+"F21.wireOp",EDGE,"E54.top"),sQuery(id+"F21.wireOp",EDGE,"E55.trimOffspring"),sQuery(id+"F21.wireOp",EDGE,"E56.trimOffspring"),sQuery(id+"F21.wireOp",EDGE,"E57.trimOffspring")])],"isStart":true})]});
            var sketch = newSketch(context, id + "F25", { "sketchPlane" : qUnion([Q0])});
            skLineSegment(sketch, "E59.bottom", {"start": v(-520, 0) * mm, "end": v(-110, 0) * mm});
            skLineSegment(sketch, "E59.top", {"start": v(-520, 1390) * mm, "end": v(-110, 1390) * mm});
            skLineSegment(sketch, "E59.left", {"start": v(-520, 0) * mm, "end": v(-520, 1390) * mm});
            skLineSegment(sketch, "E59.right", {"start": v(-110, 0) * mm, "end": v(-110, 1390) * mm});
            skLineSegment(sketch, "E60.bottom", {"start": v(-525, 1390) * mm, "end": v(-960, 1390) * mm});
            skLineSegment(sketch, "E60.top", {"start": v(-525, 0) * mm, "end": v(-960, 0) * mm});
            skLineSegment(sketch, "E60.left", {"start": v(-525, 1390) * mm, "end": v(-525, 0) * mm});
            skLineSegment(sketch, "E60.right", {"start": v(-960, 1390) * mm, "end": v(-960, 0) * mm});
            skLineSegment(sketch, "E61.bottom", {"start": v(-1074.73, 1390) * mm, "end": v(-960, 1390) * mm});
            skLineSegment(sketch, "E61.top", {"start": v(-1074.73, 1400) * mm, "end": v(-960, 1400) * mm});
            skLineSegment(sketch, "E61.left", {"start": v(-960, 1390) * mm, "end": v(-960, 1400) * mm});
            skLineSegment(sketch, "E61.right", {"start": v(-1074.73, 1390) * mm, "end": v(-1074.73, 1400) * mm});
            skLineSegment(sketch, "E62.bottom", {"start": v(-110, 1390) * mm, "end": v(-125.76, 1390) * mm});
            skLineSegment(sketch, "E62.top", {"start": v(-110, 1400) * mm, "end": v(-125.76, 1400) * mm});
            skLineSegment(sketch, "E62.left", {"start": v(-110, 1390) * mm, "end": v(-110, 1400) * mm});
            skLineSegment(sketch, "E62.right", {"start": v(-125.76, 1390) * mm, "end": v(-125.76, 1400) * mm});
            skSolve(sketch);
        }
        {
            var Q0;
            Q0 = qSketchRegion(id + "F25", true);
            extrude(context, id + "F26", {"entities" : qUnion([Q0]), "operationType" : NewBodyOperationType.ADD, "oppositeDirection" : true, "depth" : 25 * mm});
        }
    });
